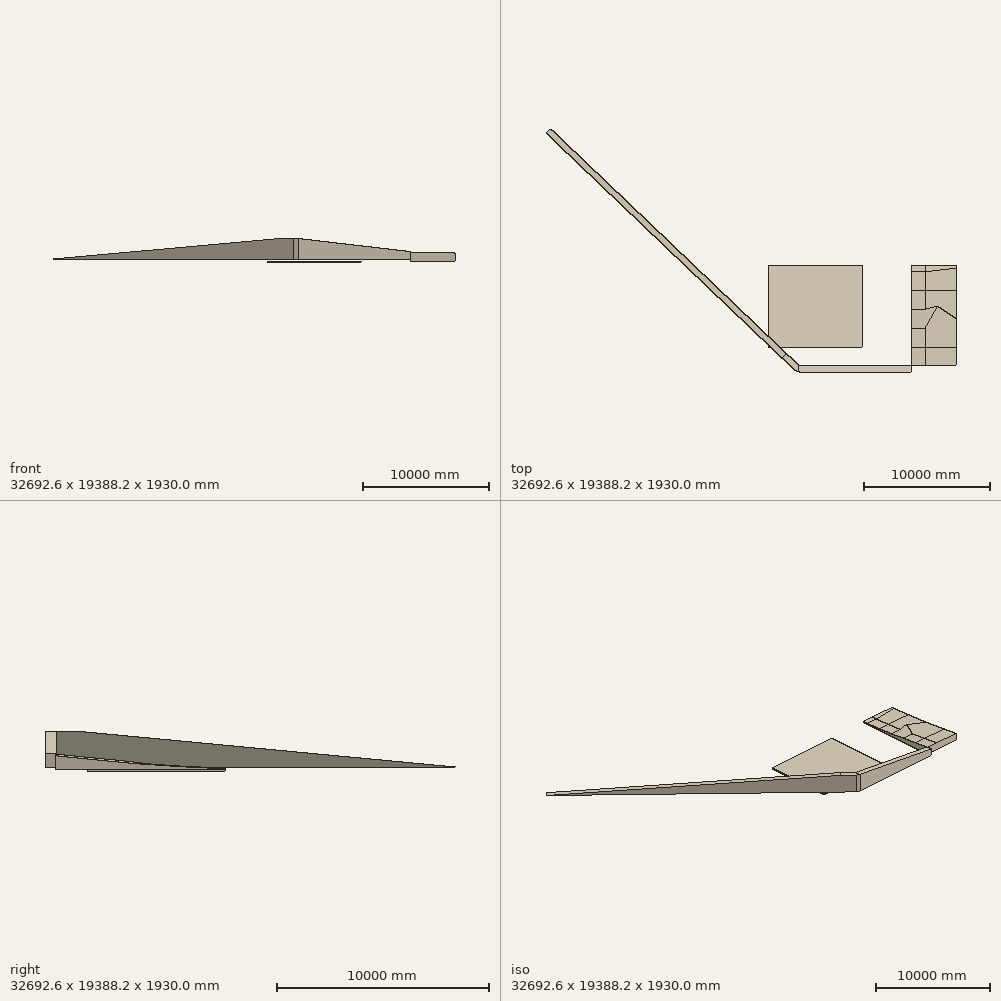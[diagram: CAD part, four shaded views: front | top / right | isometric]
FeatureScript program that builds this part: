
annotation { "Feature Type Name" : "Feature", "Feature Type Description" : "" }
export const myFeature = defineFeature(function(context is Context, id is Id, definition is map)
    precondition{}
    {
        {
            var Q0;
            Q0=qCreatedBy(makeId("Top.planeOp"),FACE);
            var sketch = newSketch(context, id + "F0", { "sketchPlane" : qUnion([Q0])});
            skLineSegment(sketch, "E0", {"start": v(0, 3398.34) * mm, "end": v(0, 70) * mm});
            skLineSegment(sketch, "E1", {"start": v(-70, 0) * mm, "end": v(-5020, 0) * mm});
            skLineSegment(sketch, "E2", {"start": v(-5020, 0) * mm, "end": v(-5020, 3000) * mm});
            skLineSegment(sketch, "E3", {"start": v(-5020, 3000) * mm, "end": v(-12500, 3000) * mm});
            skLineSegment(sketch, "E4", {"start": v(-12500, 3000) * mm, "end": v(-12500, 7455) * mm});
            skLineSegment(sketch, "E5", {"start": v(-12500, 7455) * mm, "end": v(-12924.26, 7879.26) * mm});
            skLineSegment(sketch, "E6", {"start": v(-12924.26, 7879.26) * mm, "end": v(-12924.26, 9559.26) * mm});
            skLineSegment(sketch, "E7", {"start": v(-12924.26, 9559.26) * mm, "end": v(-12500, 9983.53) * mm});
            skLineSegment(sketch, "E8", {"start": v(-12500, 9983.53) * mm, "end": v(-12500, 10813.53) * mm});
            skLineSegment(sketch, "E9", {"start": v(-12500, 10813.53) * mm, "end": v(-14013.2, 12326.74) * mm});
            skLineSegment(sketch, "E10", {"start": v(-14013.2, 12326.74) * mm, "end": v(-17113.2, 12326.74) * mm});
            skLineSegment(sketch, "E11", {"start": v(-17113.2, 12326.74) * mm, "end": v(-17113.2, 17026.74) * mm});
            skLineSegment(sketch, "E12", {"start": v(-70, 3398.34) * mm, "end": v(0, 3398.34) * mm});
            skLineSegment(sketch, "E13", {"start": v(0, -150) * mm, "end": v(-70, -150) * mm});
            skLineSegment(sketch, "E14", {"start": v(-70, -150) * mm, "end": v(-70, 0) * mm});
            skLineSegment(sketch, "E15", {"start": v(-17043.2, 11066.74) * mm, "end": v(-17043.2, 10946.74) * mm});
            skLineSegment(sketch, "E16", {"start": v(-17043.2, 10946.74) * mm, "end": v(-16923.2, 10946.74) * mm});
            skLineSegment(sketch, "E17", {"start": v(-16923.2, 10946.74) * mm, "end": v(-16923.2, 11066.74) * mm});
            skLineSegment(sketch, "E18", {"start": v(-16923.2, 11066.74) * mm, "end": v(-17043.2, 11066.74) * mm});
            skLineSegment(sketch, "E19", {"start": v(-17043.2, 17026.74) * mm, "end": v(-17113.2, 17026.74) * mm});
            skLineSegment(sketch, "E20", {"start": v(0, 0) * mm, "end": v(0, -8000) * mm});
            skSolve(sketch);
        }
        {
            var Q0;
            Q0=qCreatedBy(makeId("Right.planeOp"),FACE);
            var sketch = newSketch(context, id + "F1", { "sketchPlane" : qUnion([Q0])});
            skLineSegment(sketch, "E21", {"start": v(-8003.94, -130) * mm, "end": v(-8003.94, 613) * mm});
            skLineSegment(sketch, "E22", {"start": v(-8003.94, 0) * mm, "end": v(-6503.94, 0) * mm});
            skLineSegment(sketch, "E23", {"start": v(-6503.94, 0) * mm, "end": v(-6503.94, 458) * mm});
            skLineSegment(sketch, "E24", {"start": v(-6503.94, 458) * mm, "end": v(-8003.94, 613) * mm});
            skLineSegment(sketch, "E25", {"start": v(-6503.94, 0) * mm, "end": v(-5003.94, 0) * mm});
            skLineSegment(sketch, "E26", {"start": v(-5003.94, 0) * mm, "end": v(-5003.94, 313) * mm});
            skLineSegment(sketch, "E27", {"start": v(-5003.94, 313) * mm, "end": v(-6503.94, 458) * mm});
            skLineSegment(sketch, "E28", {"start": v(-5003.94, 0) * mm, "end": v(-3503.94, 0) * mm});
            skLineSegment(sketch, "E29", {"start": v(-3503.94, 0) * mm, "end": v(-3503.94, 140) * mm});
            skLineSegment(sketch, "E30", {"start": v(-3503.94, 140) * mm, "end": v(-5003.94, 313) * mm});
            skLineSegment(sketch, "E31", {"start": v(-3503.94, 0) * mm, "end": v(-2003.94, 0) * mm});
            skLineSegment(sketch, "E32", {"start": v(-2003.94, 0) * mm, "end": v(-2003.94, 40) * mm});
            skLineSegment(sketch, "E33", {"start": v(-2003.94, 40) * mm, "end": v(-3503.94, 140) * mm});
            skLineSegment(sketch, "E34", {"start": v(-503.94, 0) * mm, "end": v(-503.94, -30) * mm});
            skLineSegment(sketch, "E35", {"start": v(-503.94, -30) * mm, "end": v(0, 0) * mm});
            skLineSegment(sketch, "E36", {"start": v(-503.94, -30) * mm, "end": v(-2003.94, 40) * mm});
            skLineSegment(sketch, "E37", {"start": v(0, 0) * mm, "end": v(0, -130) * mm});
            skLineSegment(sketch, "E38", {"start": v(0, -130) * mm, "end": v(-8003.94, -130) * mm});
            skSolve(sketch);
        }
        {
            var Q0;
            {var subQ2=sQuery(id+"F1.wireOp",EDGE,"E22");Q0=makeQuery(id+"F1.imprint","IMPRINT",FACE,{"disambiguationData":[TD([[makeQuery(id+"F1.imprint","IMPRINT",EDGE,{"derivedFrom":subQ2}),1.0]])]});}
            var Q1;
            Q1=makeQuery(id+"F1.imprint","IMPRINT",FACE,{"disambiguationData":[TD([[makeQuery(id+"F1.imprint","IMPRINT",EDGE,{"derivedFrom":sQuery(id+"F1.wireOp",EDGE,"E23")}),-1.0]])]});
            var Q2;
            Q2=makeQuery(id+"F1.imprint","IMPRINT",FACE,{"disambiguationData":[TD([[makeQuery(id+"F1.imprint","IMPRINT",EDGE,{"derivedFrom":sQuery(id+"F1.wireOp",EDGE,"E26")}),-1.0]])]});
            var Q3;
            Q3=makeQuery(id+"F1.imprint","IMPRINT",FACE,{"disambiguationData":[TD([[makeQuery(id+"F1.imprint","IMPRINT",EDGE,{"derivedFrom":sQuery(id+"F1.wireOp",EDGE,"E29")}),-1.0]])]});
            var Q4;
            {var subQ0=sQuery(id+"F1.wireOp",EDGE,"E22");Q4=makeQuery(id+"F1.imprint","IMPRINT",FACE,{"disambiguationData":[TD([[makeQuery(id+"F1.imprint","IMPRINT",EDGE,{"derivedFrom":subQ0}),-1.0]])]});}
            extrude(context, id + "F2", {"entities" : qUnion([Q0, Q1, Q2, Q3, Q4]), "depth" : 2500 * mm, "offsetDistance" : 25 * mm});
        }
        {
            var Q0;
            Q0=makeQuery(id+"F2.opExtrude","CAP_EDGE",EDGE,{"disambiguationData":[OSD([sQuery(id+"F1.wireOp",EDGE,"E24")])],"isStart":false});
            var Q1;
            Q1=makeQuery(id+"F2.opExtrude","CAP_EDGE",EDGE,{"disambiguationData":[OSD([sQuery(id+"F1.wireOp",EDGE,"E27")])],"isStart":false});
            chamfer(context, id + "F3", {"entities" : qUnion([Q0, Q1]), "chamferType" : ChamferType.TWO_OFFSETS, "width1" : 80 * mm, "oppositeDirection" : false, "width2" : 2500 * mm, "tangentPropagation" : true});
        }
        {
            var Q0;
            Q0=makeQuery(id+"F2.opExtrude","CAP_EDGE",EDGE,{"disambiguationData":[OSD([sQuery(id+"F1.wireOp",EDGE,"E36")])],"isStart":false});
            var Q1;
            Q1=makeQuery(id+"F2.opExtrude","CAP_EDGE",EDGE,{"disambiguationData":[OSD([sQuery(id+"F1.wireOp",EDGE,"E35")])],"isStart":false});
            var Q2;
            Q2=makeQuery(id+"F2.opExtrude","CAP_EDGE",EDGE,{"disambiguationData":[OSD([sQuery(id+"F1.wireOp",EDGE,"E33")])],"isStart":false});
            chamfer(context, id + "F4", {"entities" : qUnion([Q0, Q1, Q2]), "chamferType" : ChamferType.TWO_OFFSETS, "width1" : 30 * mm, "oppositeDirection" : false, "width2" : 2500 * mm, "tangentPropagation" : true});
        }
        {
            var Q0;
            Q0=makeQuery(id+"F2.opExtrude","CAP_FACE",FACE,{"disambiguationData":[OSD([sQuery(id+"F1.wireOp",EDGE,"E21"),sQuery(id+"F1.wireOp",EDGE,"E24"),sQuery(id+"F1.wireOp",EDGE,"E27"),sQuery(id+"F1.wireOp",EDGE,"E30"),sQuery(id+"F1.wireOp",EDGE,"E33"),sQuery(id+"F1.wireOp",EDGE,"E35"),sQuery(id+"F1.wireOp",EDGE,"E36"),sQuery(id+"F1.wireOp",EDGE,"E37"),sQuery(id+"F1.wireOp",EDGE,"E38")])],"isStart":true});
            extrude(context, id + "F5", {"entities" : qUnion([Q0]), "operationType" : NewBodyOperationType.ADD, "depth" : 1100 * mm, "offsetDistance" : 25 * mm});
        }
        {
            var Q0;
            {var subQ0=sQuery(id+"F1.wireOp",EDGE,"E35");Q0=makeQuery(id+"F4.opChamfer","BLEND_EDGE",EDGE,{"blendedFrom":[makeQuery(id+"F2.opExtrude","CAP_EDGE",EDGE,{"disambiguationData":[OSD([subQ0])],"isStart":false}),makeQuery(id+"F2.opExtrude","CAP_FACE",FACE,{"disambiguationData":[OSD([sQuery(id+"F1.wireOp",EDGE,"E21"),sQuery(id+"F1.wireOp",EDGE,"E24"),sQuery(id+"F1.wireOp",EDGE,"E27"),sQuery(id+"F1.wireOp",EDGE,"E30"),sQuery(id+"F1.wireOp",EDGE,"E33"),subQ0,sQuery(id+"F1.wireOp",EDGE,"E36"),sQuery(id+"F1.wireOp",EDGE,"E37"),sQuery(id+"F1.wireOp",EDGE,"E38")])],"isStart":false})],"blendedInto":[makeQuery(id+"F2.opExtrude","CAP_FACE",FACE,{"disambiguationData":[OSD([sQuery(id+"F1.wireOp",EDGE,"E21"),sQuery(id+"F1.wireOp",EDGE,"E24"),sQuery(id+"F1.wireOp",EDGE,"E27"),sQuery(id+"F1.wireOp",EDGE,"E30"),sQuery(id+"F1.wireOp",EDGE,"E33"),subQ0,sQuery(id+"F1.wireOp",EDGE,"E36"),sQuery(id+"F1.wireOp",EDGE,"E37"),sQuery(id+"F1.wireOp",EDGE,"E38")])],"isStart":false})]});}
            chamfer(context, id + "F6", {"entities" : qUnion([Q0]), "chamferType" : ChamferType.TWO_OFFSETS, "width1" : 30 * mm, "oppositeDirection" : false, "width2" : 2500 * mm, "tangentPropagation" : true});
        }
        {
            var Q0;
            Q0=qCreatedBy(makeId("Top.planeOp"),FACE);
            cPlane(context, id + "F7", {"entities" : qUnion([Q0]), "cplaneType" : CPlaneType.OFFSET, "offset" : 130 * mm, "oppositeDirection" : true, "width" : 150 * mm, "height" : 150 * mm});
        }
        {
            var Q0;
            Q0=qCreatedBy(id+"F7.planeOp",FACE);
            var sketch = newSketch(context, id + "F8", { "sketchPlane" : qUnion([Q0])});
            skLineSegment(sketch, "E39", {"start": v(-5020, 0) * mm, "end": v(-5020, -6500) * mm});
            skLineSegment(sketch, "E40", {"start": v(-5020, -6500) * mm, "end": v(-12500, -6500) * mm});
            skLineSegment(sketch, "E41", {"start": v(-5020, 0) * mm, "end": v(-12500, 0) * mm});
            skLineSegment(sketch, "E42", {"start": v(-12500, 0) * mm, "end": v(-12500, -6500) * mm});
            skSolve(sketch);
        }
        {
            var Q0;
            Q0=makeQuery(id+"F8.imprint","IMPRINT",FACE,{"disambiguationData":[TD([[makeQuery(id+"F8.imprint","IMPRINT",EDGE,{"derivedFrom":sQuery(id+"F8.wireOp",EDGE,"E39")}),-1.0]])]});
            extrude(context, id + "F9", {"entities" : qUnion([Q0]), "oppositeDirection" : true, "depth" : 100 * mm, "offsetDistance" : 25 * mm});
        }
        {
            var Q0;
            Q0=qCreatedBy(makeId("Top.planeOp"),FACE);
            var sketch = newSketch(context, id + "F10", { "sketchPlane" : qUnion([Q0])});
            skLineSegment(sketch, "E43", {"start": v(0, 0) * mm, "end": v(0, -8000) * mm});
            skLineSegment(sketch, "E44", {"start": v(0, -8000) * mm, "end": v(-10040, -8000) * mm});
            skLineSegment(sketch, "E45", {"start": v(-10040, -8500) * mm, "end": v(-1108.46, -8500) * mm});
            skLineSegment(sketch, "E46", {"start": v(-1108.46, -8500) * mm, "end": v(-1108.46, -8000) * mm});
            skLineSegment(sketch, "E47", {"start": v(-10040, -8000) * mm, "end": v(-10040, 8830.93) * mm});
            skLineSegment(sketch, "E48", {"start": v(-10040, 8830.93) * mm, "end": v(-16991.2, 8830.93) * mm});
            skLineSegment(sketch, "E49", {"start": v(-16991.2, 8830.93) * mm, "end": v(-16991.2, 10888.2) * mm});
            skLineSegment(sketch, "E50", {"start": v(-5054.43, 10888.2) * mm, "end": v(-16991.2, 10888.2) * mm});
            skLineSegment(sketch, "E51", {"start": v(-5054.43, 10888.2) * mm, "end": v(-5054.43, 10945.2) * mm});
            skLineSegment(sketch, "E52", {"start": v(-17042, 10945.16) * mm, "end": v(-29847.55, 10888.2) * mm});
            skLineSegment(sketch, "E53", {"start": v(-29847.55, 10888.2) * mm, "end": v(-10040, -8000) * mm});
            skLineSegment(sketch, "E54.0", {"start": v(-30192.6, 10526.35) * mm, "end": v(-10385.06, -8361.85) * mm});
            skLineSegment(sketch, "E55", {"start": v(-30192.6, 10526.35) * mm, "end": v(-29847.55, 10888.2) * mm});
            skLineSegment(sketch, "E56", {"start": v(-10385.06, -8361.85) * mm, "end": v(-10040, -8500) * mm});
            skSolve(sketch);
        }
        {
            var Q0;
            {var subQ0=sQuery(id+"F10.wireOp",EDGE,"CCjcnuVb-JPbw-6IGW-6baz-O8KAafd430pA");Q0=makeQuery(id+"F10.imprint","IMPRINT",FACE,{"disambiguationData":[TD([[makeQuery(id+"F10.imprint","IMPRINT",EDGE,{"derivedFrom":subQ0}),1.0]])]});}
            var Q1;
            Q1=makeQuery(id+"F10.imprint","IMPRINT",FACE,{"disambiguationData":[TD([[makeQuery(id+"F10.imprint","IMPRINT",EDGE,{"derivedFrom":sQuery(id+"F10.wireOp",EDGE,"E45")}),1.0]])]});
            extrude(context, id + "F11", {"entities" : qUnion([Q0, Q1]), "depth" : 1700 * mm, "offsetDistance" : 25 * mm});
        }
        {
            var Q0;
            Q0=makeQuery(id+"F11.opExtrude","CAP_EDGE",EDGE,{"disambiguationData":[OSD([sQuery(id+"F10.wireOp",EDGE,"E46")])],"isStart":false});
            chamfer(context, id + "F12", {"entities" : qUnion([Q0]), "chamferType" : ChamferType.TWO_OFFSETS, "width1" : 1050 * mm, "oppositeDirection" : true, "width2" : 9000 * mm, "tangentPropagation" : true});
        }
        {
            var Q0;
            Q0=makeQuery(id+"F11.opExtrude","CAP_EDGE",EDGE,{"disambiguationData":[OSD([sQuery(id+"F10.wireOp",EDGE,"E55")])],"isStart":false});
            chamfer(context, id + "F13", {"entities" : qUnion([Q0]), "chamferType" : ChamferType.TWO_OFFSETS, "width1" : 1700 * mm, "oppositeDirection" : false, "width2" : 26000 * mm, "tangentPropagation" : true});
        }
    });
